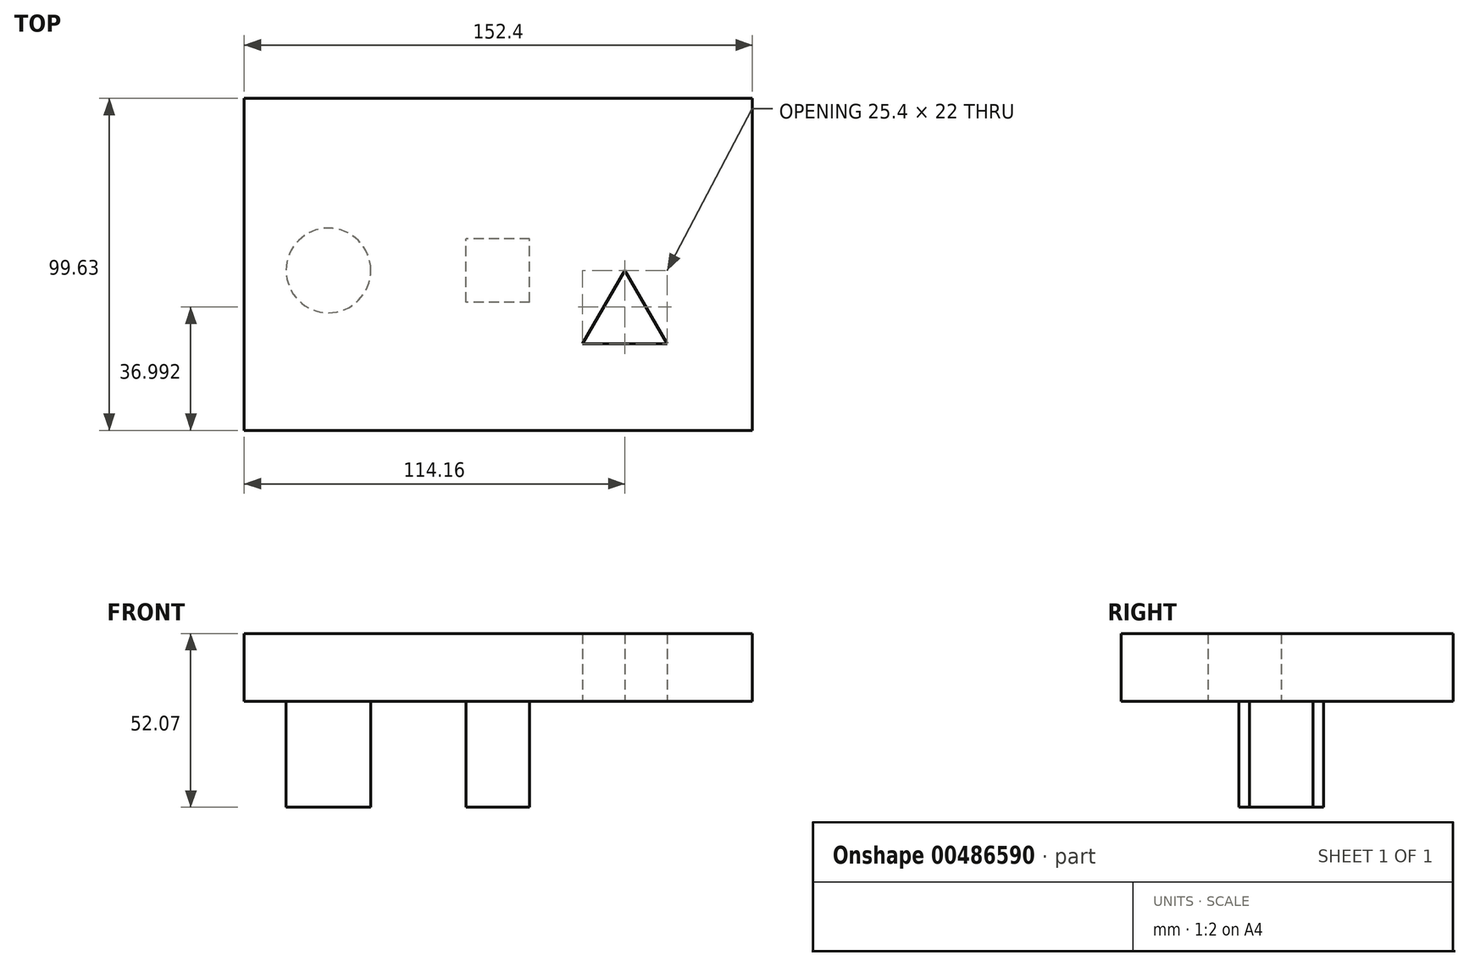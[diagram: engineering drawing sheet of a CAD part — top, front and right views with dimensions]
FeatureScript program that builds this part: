
annotation { "Feature Type Name" : "Feature", "Feature Type Description" : "" }
export const myFeature = defineFeature(function(context is Context, id is Id, definition is map)
    precondition{}
    {
        {
            var Q0;
            Q0=qCreatedBy(makeId("Top.planeOp"),FACE);
            var sketch = newSketch(context, id + "F0", { "sketchPlane" : qUnion([Q0])});
            skPoint(sketch, "E0.middle", {"position": v(0, 0) * mm});
            skLineSegment(sketch, "E1", {"start": v(0.14, -47.99) * mm, "end": v(44.59, -47.99) * mm});
            skLineSegment(sketch, "E2.bottom", {"start": v(44.59, -47.99) * mm, "end": v(-107.81, -47.99) * mm});
            skLineSegment(sketch, "E2.top", {"start": v(44.59, 51.64) * mm, "end": v(-107.81, 51.64) * mm});
            skLineSegment(sketch, "E2.left", {"start": v(44.59, -47.99) * mm, "end": v(44.59, 51.64) * mm});
            skLineSegment(sketch, "E2.right", {"start": v(-107.81, -47.99) * mm, "end": v(-107.81, 51.64) * mm});
            skLineSegment(sketch, "E3", {"start": v(0, 0) * mm, "end": v(6.35, 0) * mm});
            skLineSegment(sketch, "E4", {"start": v(6.35, 0) * mm, "end": v(-6.35, -22) * mm});
            skLineSegment(sketch, "E5", {"start": v(-6.35, -22) * mm, "end": v(19.05, -22) * mm});
            skLineSegment(sketch, "E6", {"start": v(19.05, -22) * mm, "end": v(6.35, 0) * mm});
            skLineSegment(sketch, "E7", {"start": v(0, -27.65) * mm, "end": v(-31.75, -27.65) * mm});
            skLineSegment(sketch, "E8", {"start": v(-31.75, -27.65) * mm, "end": v(-31.75, 0) * mm});
            skLineSegment(sketch, "E9.bottom", {"start": v(-22.23, -9.53) * mm, "end": v(-41.27, -9.52) * mm});
            skLineSegment(sketch, "E9.top", {"start": v(-22.23, 9.53) * mm, "end": v(-41.27, 9.53) * mm});
            skLineSegment(sketch, "E9.left", {"start": v(-22.23, -9.52) * mm, "end": v(-22.22, 9.53) * mm});
            skLineSegment(sketch, "E9.right", {"start": v(-41.27, -9.52) * mm, "end": v(-41.27, 9.53) * mm});
            skPoint(sketch, "E9.middle", {"position": v(-31.75, 0) * mm});
            skLineSegment(sketch, "E10", {"start": v(-31.75, -27.65) * mm, "end": v(-82.55, -27.65) * mm});
            skLineSegment(sketch, "E11", {"start": v(-82.55, -27.65) * mm, "end": v(-82.55, 0) * mm});
            skCircle(sketch, "E12", {"center": v(-82.55, 0) * mm, "radius": 12.7 * mm});
            skSolve(sketch);
        }
        {
            var Q0;
            Q0=makeQuery(id+"F0.imprint","IMPRINT",FACE,{"disambiguationData":[TD([[makeQuery(id+"F0.imprint","IMPRINT",EDGE,{"derivedFrom":sQuery(id+"F0.wireOp",EDGE,"E2.top")}),1.0]])]});
            var Q1;
            Q1=makeQuery(id+"F0.imprint","IMPRINT",FACE,{"disambiguationData":[TD([[makeQuery(id+"F0.imprint","IMPRINT",EDGE,{"derivedFrom":sQuery(id+"F0.wireOp",EDGE,"E12")}),1.0]])]});
            var Q2;
            Q2=makeQuery(id+"F0.imprint","IMPRINT",FACE,{"disambiguationData":[TD([[makeQuery(id+"F0.imprint","IMPRINT",EDGE,{"derivedFrom":sQuery(id+"F0.wireOp",EDGE,"E9.top")}),1.0]])]});
            extrude(context, id + "F1", {"entities" : qUnion([Q0, Q1, Q2]), "depth" : 20.32 * mm});
        }
        {
            var Q0;
            Q0=makeQuery(id+"F0.imprint","IMPRINT",FACE,{"disambiguationData":[TD([[makeQuery(id+"F0.imprint","IMPRINT",EDGE,{"derivedFrom":sQuery(id+"F0.wireOp",EDGE,"E12")}),1.0]])]});
            var Q1;
            Q1=makeQuery(id+"F0.imprint","IMPRINT",FACE,{"disambiguationData":[TD([[makeQuery(id+"F0.imprint","IMPRINT",EDGE,{"derivedFrom":sQuery(id+"F0.wireOp",EDGE,"E9.top")}),1.0]])]});
            extrude(context, id + "F2", {"entities" : qUnion([Q0, Q1]), "operationType" : NewBodyOperationType.ADD, "oppositeDirection" : true, "depth" : 31.75 * mm});
        }
    });
